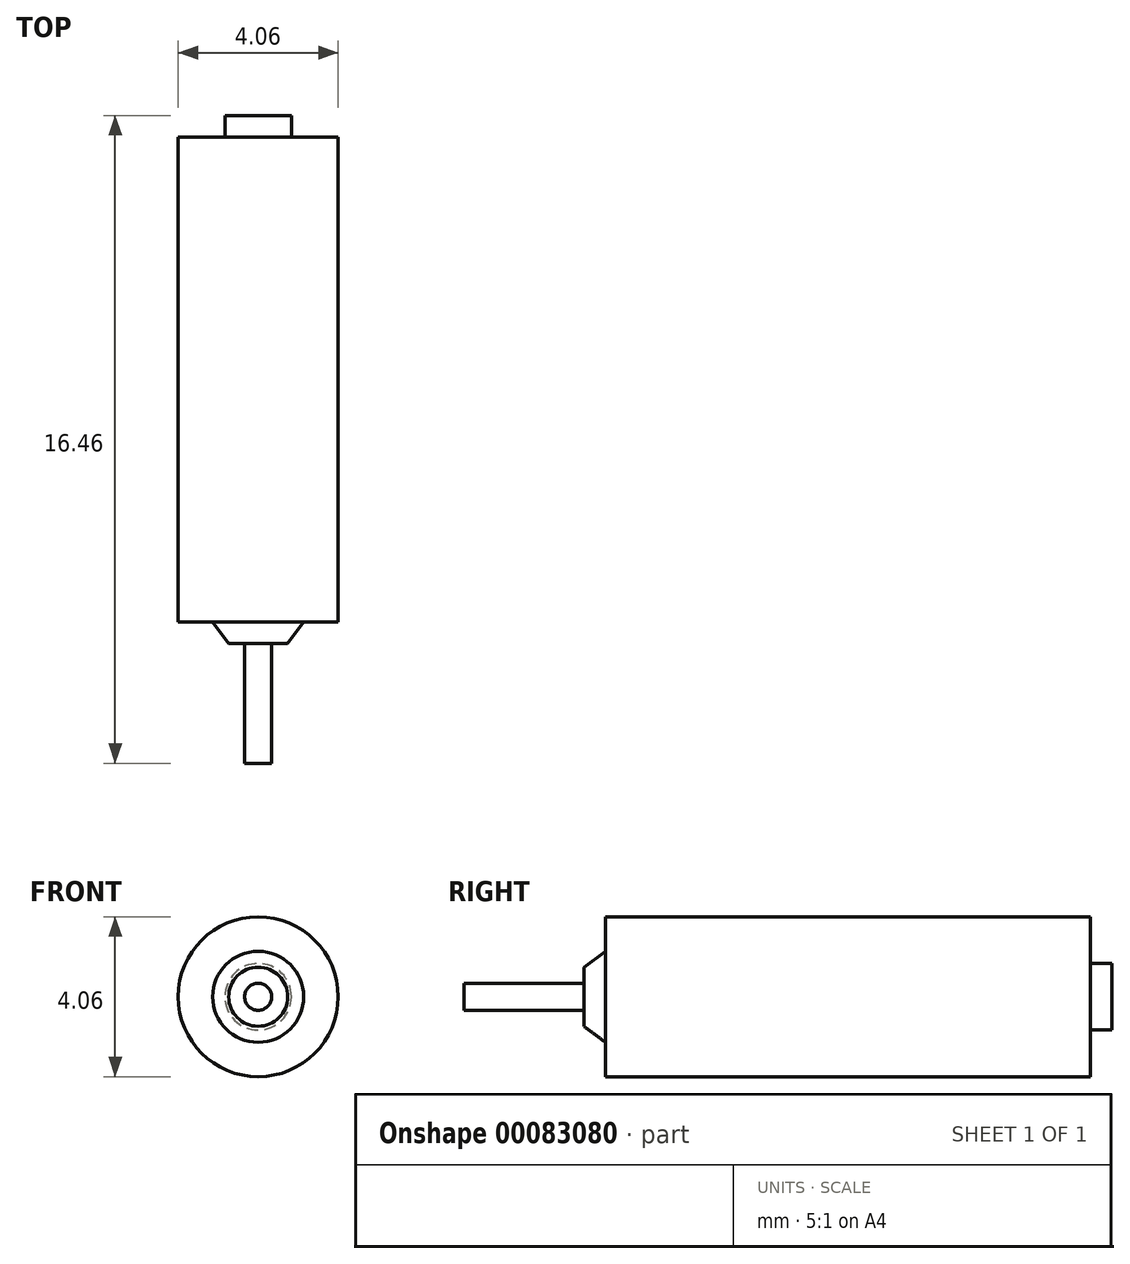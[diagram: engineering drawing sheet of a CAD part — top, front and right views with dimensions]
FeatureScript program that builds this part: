
annotation { "Feature Type Name" : "Feature", "Feature Type Description" : "" }
export const myFeature = defineFeature(function(context is Context, id is Id, definition is map)
    precondition{}
    {
        {
            var Q0;
            Q0=qCreatedBy(makeId("Front.planeOp"),FACE);
            var sketch = newSketch(context, id + "F0", { "sketchPlane" : qUnion([Q0])});
            skCircle(sketch, "E0", {"center": v(0, 0) * mm, "radius": 2.03 * mm});
            skSolve(sketch);
        }
        {
            var Q0;
            Q0=makeQuery(id+"F0.imprint","IMPRINT",FACE,{"disambiguationData":[TD([[makeQuery(id+"F0.imprint","IMPRINT",EDGE,{"derivedFrom":sQuery(id+"F0.wireOp",EDGE,"E0")}),1.0]])]});
            extrude(context, id + "F1", {"entities" : qUnion([Q0]), "oppositeDirection" : true, "depth" : 12.32 * mm});
        }
        {
            var Q0;
            Q0=makeQuery(id+"F1.opExtrude","CAP_FACE",FACE,{"disambiguationData":[OSD([sQuery(id+"F0.wireOp",EDGE,"E0")])],"isStart":false});
            var sketch = newSketch(context, id + "F2", { "sketchPlane" : qUnion([Q0])});
            skCircle(sketch, "E1", {"center": v(0, 0) * mm, "radius": 0.84 * mm});
            skSolve(sketch);
        }
        {
            var Q0;
            Q0=makeQuery(id+"F2.imprint","IMPRINT",FACE,{"disambiguationData":[TD([[makeQuery(id+"F2.imprint","IMPRINT",EDGE,{"derivedFrom":sQuery(id+"F2.wireOp",EDGE,"E1")}),1.0]])]});
            extrude(context, id + "F3", {"entities" : qUnion([Q0]), "operationType" : NewBodyOperationType.ADD, "depth" : 0.55 * mm});
        }
        {
            var Q0;
            Q0=makeQuery(id+"F1.opExtrude","CAP_FACE",FACE,{"disambiguationData":[OSD([sQuery(id+"F0.wireOp",EDGE,"E0")])],"isStart":true});
            var sketch = newSketch(context, id + "F4", { "sketchPlane" : qUnion([Q0])});
            skCircle(sketch, "E2", {"center": v(0, 0) * mm, "radius": 1.16 * mm});
            skSolve(sketch);
        }
        {
            var Q0;
            Q0=qCreatedBy(makeId("Front.planeOp"),FACE);
            cPlane(context, id + "F5", {"entities" : qUnion([Q0]), "cplaneType" : CPlaneType.OFFSET, "offset" : 0.55 * mm, "width" : 152.4 * mm, "height" : 152.4 * mm});
        }
        {
            var Q0;
            Q0=qCreatedBy(id+"F5.planeOp",FACE);
            var sketch = newSketch(context, id + "F6", { "sketchPlane" : qUnion([Q0])});
            skCircle(sketch, "E3", {"center": v(0, 0) * mm, "radius": 0.75 * mm});
            skSolve(sketch);
        }
        {
            var Q1;
            Q1=makeQuery(id+"F4.imprint","IMPRINT",FACE,{"disambiguationData":[TD([[makeQuery(id+"F4.imprint","IMPRINT",EDGE,{"derivedFrom":sQuery(id+"F4.wireOp",EDGE,"E2")}),1.0]])]});
            var Q2;
            Q2=makeQuery(id+"F6.imprint","IMPRINT",FACE,{"disambiguationData":[TD([[makeQuery(id+"F6.imprint","IMPRINT",EDGE,{"derivedFrom":sQuery(id+"F6.wireOp",EDGE,"E3")}),1.0]])]});
            loft(context, id + "F7", {"operationType" : NewBodyOperationType.ADD, "sheetProfilesArray" : [{ "sheetProfileEntities" : qUnion([Q1]) }, { "sheetProfileEntities" : qUnion([Q2]) }]});
        }
        {
            var Q0;
            Q0=makeQuery(id+"F7.opLoft","CAP_FACE",FACE,{"disambiguationData":[OSD([makeQuery(id+"F6.imprint","IMPRINT",FACE,{"disambiguationData":[TD([[makeQuery(id+"F6.imprint","IMPRINT",EDGE,{"derivedFrom":sQuery(id+"F6.wireOp",EDGE,"E3")}),1.0]])]})])],"isStart":true});
            var sketch = newSketch(context, id + "F8", { "sketchPlane" : qUnion([Q0])});
            skCircle(sketch, "E4", {"center": v(0, 0) * mm, "radius": 0.34 * mm});
            skSolve(sketch);
        }
        {
            var Q0;
            Q0=makeQuery(id+"F8.imprint","IMPRINT",FACE,{"disambiguationData":[TD([[makeQuery(id+"F8.imprint","IMPRINT",EDGE,{"derivedFrom":sQuery(id+"F8.wireOp",EDGE,"E4")}),1.0]])]});
            extrude(context, id + "F9", {"entities" : qUnion([Q0]), "operationType" : NewBodyOperationType.ADD, "depth" : 3.05 * mm});
        }
    });
